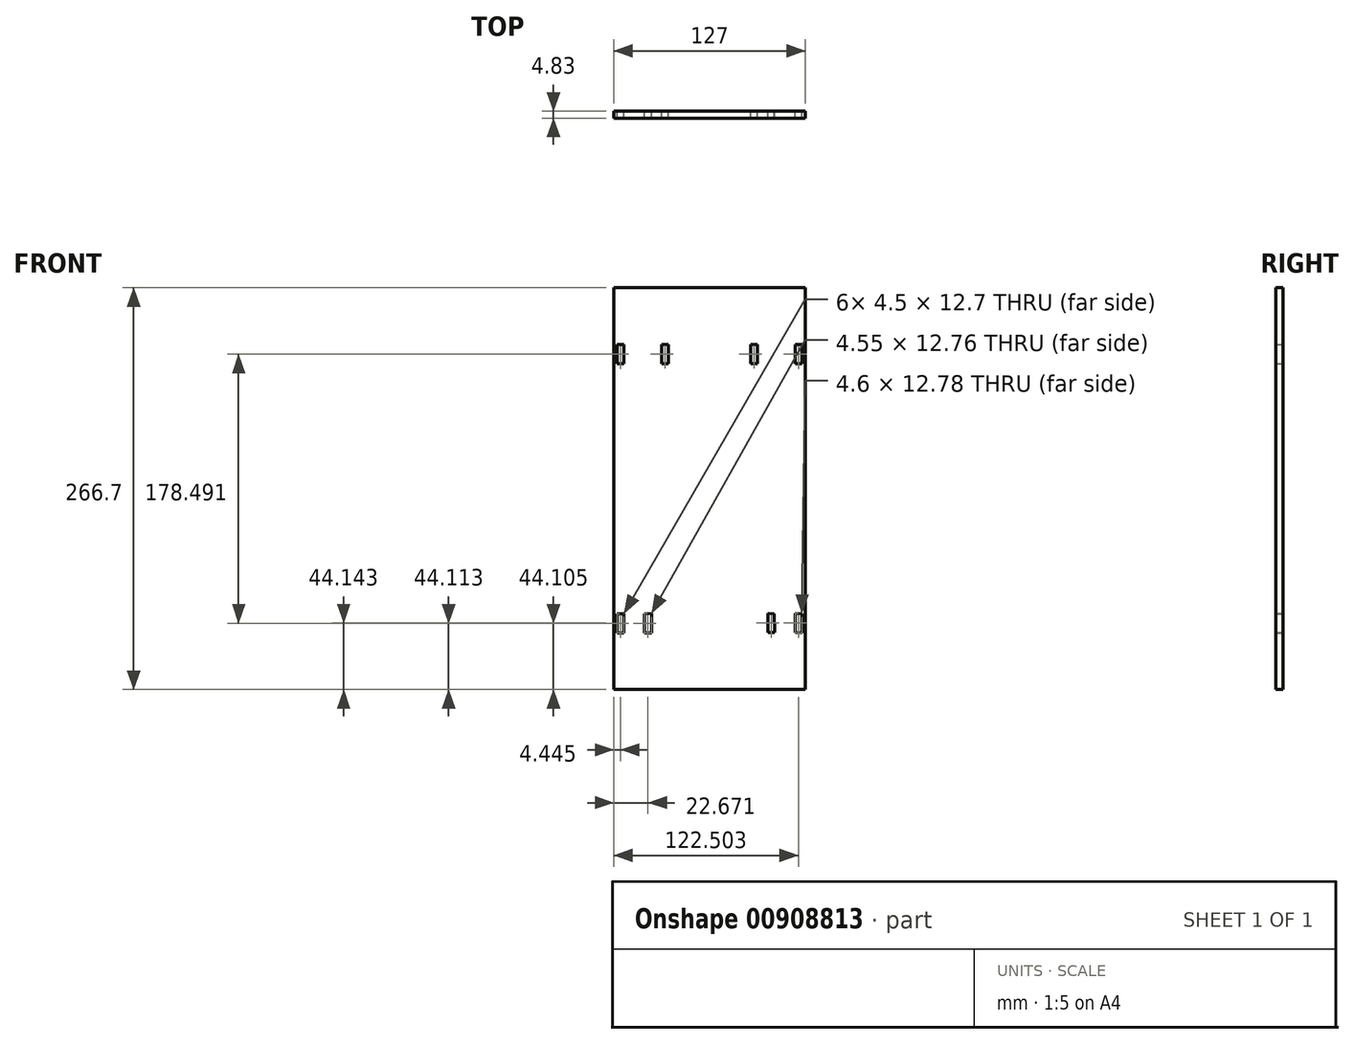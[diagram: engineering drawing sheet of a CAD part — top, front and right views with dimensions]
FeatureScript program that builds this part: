
annotation { "Feature Type Name" : "Feature", "Feature Type Description" : "" }
export const myFeature = defineFeature(function(context is Context, id is Id, definition is map)
    precondition{}
    {
        {
            var Q0;
            Q0=qCreatedBy(makeId("Front.planeOp"),FACE);
            var sketch = newSketch(context, id + "F0", { "sketchPlane" : qUnion([Q0])});
            skLineSegment(sketch, "E0.bottom", {"start": v(63.5, -100.58) * mm, "end": v(-63.5, -100.58) * mm});
            skLineSegment(sketch, "E0.top", {"start": v(63.5, 166.12) * mm, "end": v(-63.5, 166.12) * mm});
            skLineSegment(sketch, "E0.left", {"start": v(63.5, -100.58) * mm, "end": v(63.5, 166.12) * mm});
            skLineSegment(sketch, "E0.right", {"start": v(-63.5, -100.58) * mm, "end": v(-63.5, 166.12) * mm});
            skLineSegment(sketch, "E1.bottom", {"start": v(-61.3, 115.67) * mm, "end": v(-56.8, 115.67) * mm});
            skLineSegment(sketch, "E1.top", {"start": v(-61.3, 128.37) * mm, "end": v(-56.8, 128.37) * mm});
            skLineSegment(sketch, "E1.left", {"start": v(-61.3, 115.67) * mm, "end": v(-61.3, 128.37) * mm});
            skLineSegment(sketch, "E1.right", {"start": v(-56.8, 115.67) * mm, "end": v(-56.8, 128.37) * mm});
            skPoint(sketch, "E1.middle", {"position": v(-59.05, 122.02) * mm});
            skPoint(sketch, "E2", {"position": v(-63.5, 32.77) * mm});
            skPoint(sketch, "E3", {"position": v(-63.5, 99.44) * mm});
            skPoint(sketch, "E4", {"position": v(-63.5, -33.9) * mm});
            skPoint(sketch, "E5", {"position": v(63.5, 32.77) * mm});
            skPoint(sketch, "E6", {"position": v(63.5, 99.44) * mm});
            skPoint(sketch, "E7", {"position": v(63.5, -33.9) * mm});
            skLineSegment(sketch, "E8.MirrorCS", {"start": v(61.3, 128.37) * mm, "end": v(56.8, 128.37) * mm});
            skLineSegment(sketch, "E9.MirrorCS", {"start": v(61.3, 115.67) * mm, "end": v(61.3, 128.37) * mm});
            skLineSegment(sketch, "E10.MirrorCS", {"start": v(56.8, 115.67) * mm, "end": v(56.8, 128.37) * mm});
            skLineSegment(sketch, "E11.MirrorCS", {"start": v(61.3, 115.67) * mm, "end": v(56.8, 115.67) * mm});
            skLineSegment(sketch, "E12.MirrorCS", {"start": v(-61.3, -62.83) * mm, "end": v(-56.8, -62.83) * mm});
            skLineSegment(sketch, "E13.MirrorCS", {"start": v(-61.3, -50.13) * mm, "end": v(-61.3, -62.83) * mm});
            skLineSegment(sketch, "E14.MirrorCS", {"start": v(-56.8, -50.13) * mm, "end": v(-56.8, -62.83) * mm});
            skLineSegment(sketch, "E15.MirrorCS", {"start": v(-61.3, -50.13) * mm, "end": v(-56.8, -50.13) * mm});
            skLineSegment(sketch, "E16.MirrorCS", {"start": v(56.7, -50.05) * mm, "end": v(56.86, -62.75) * mm});
            skLineSegment(sketch, "E17.MirrorCS", {"start": v(61.3, -62.83) * mm, "end": v(56.86, -62.75) * mm});
            skLineSegment(sketch, "E18.MirrorCS", {"start": v(61.3, -50.13) * mm, "end": v(61.3, -62.83) * mm});
            skLineSegment(sketch, "E19.MirrorCS", {"start": v(61.3, -50.13) * mm, "end": v(56.7, -50.05) * mm});
            skLineSegment(sketch, "E20.bottom", {"start": v(-31.7, 115.88) * mm, "end": v(-27.2, 115.88) * mm});
            skLineSegment(sketch, "E20.top", {"start": v(-31.7, 128.58) * mm, "end": v(-27.2, 128.58) * mm});
            skLineSegment(sketch, "E20.left", {"start": v(-31.7, 115.88) * mm, "end": v(-31.7, 128.58) * mm});
            skLineSegment(sketch, "E20.right", {"start": v(-27.2, 115.88) * mm, "end": v(-27.2, 128.58) * mm});
            skLineSegment(sketch, "E21.MirrorCS", {"start": v(31.7, 128.58) * mm, "end": v(27.2, 128.58) * mm});
            skLineSegment(sketch, "E22.MirrorCS", {"start": v(31.7, 115.88) * mm, "end": v(31.7, 128.58) * mm});
            skLineSegment(sketch, "E23.MirrorCS", {"start": v(27.2, 115.88) * mm, "end": v(27.2, 128.58) * mm});
            skLineSegment(sketch, "E24.MirrorCS", {"start": v(31.7, 115.88) * mm, "end": v(27.2, 115.88) * mm});
            skLineSegment(sketch, "E25.MirrorCS", {"start": v(-43.1, -50.15) * mm, "end": v(-38.55, -50.09) * mm});
            skLineSegment(sketch, "E26.MirrorCS", {"start": v(-38.55, -50.09) * mm, "end": v(-38.55, -62.85) * mm});
            skLineSegment(sketch, "E27.MirrorCS", {"start": v(-43.1, -62.85) * mm, "end": v(-38.55, -62.85) * mm});
            skLineSegment(sketch, "E28.MirrorCS", {"start": v(-43.1, -50.15) * mm, "end": v(-43.1, -62.85) * mm});
            skLineSegment(sketch, "E29.MirrorCS", {"start": v(43, -50.15) * mm, "end": v(43.16, -62.74) * mm});
            skLineSegment(sketch, "E30.MirrorCS", {"start": v(38.66, -50.04) * mm, "end": v(38.66, -62.74) * mm});
            skLineSegment(sketch, "E31.MirrorCS", {"start": v(43.16, -62.74) * mm, "end": v(38.66, -62.74) * mm});
            skLineSegment(sketch, "E32.MirrorCS", {"start": v(43, -50.15) * mm, "end": v(38.66, -50.04) * mm});
            skSolve(sketch);
        }
        {
            var Q0;
            Q0=makeQuery(id+"F0.imprint","IMPRINT",FACE,{"disambiguationData":[TD([[makeQuery(id+"F0.imprint","IMPRINT",EDGE,{"derivedFrom":sQuery(id+"F0.wireOp",EDGE,"E1.bottom")}),-1.0]])]});
            var Q1;
            Q1=makeQuery(id+"F0.imprint","IMPRINT",FACE,{"disambiguationData":[TD([[makeQuery(id+"F0.imprint","IMPRINT",EDGE,{"derivedFrom":sQuery(id+"F0.wireOp",EDGE,"E8.MirrorCS")}),-1.0]])]});
            var Q2;
            Q2=makeQuery(id+"F0.imprint","IMPRINT",FACE,{"disambiguationData":[TD([[makeQuery(id+"F0.imprint","IMPRINT",EDGE,{"derivedFrom":sQuery(id+"F0.wireOp",EDGE,"E16.MirrorCS")}),-1.0]])]});
            var Q3;
            Q3=makeQuery(id+"F0.imprint","IMPRINT",FACE,{"disambiguationData":[TD([[makeQuery(id+"F0.imprint","IMPRINT",EDGE,{"derivedFrom":sQuery(id+"F0.wireOp",EDGE,"E12.MirrorCS")}),-1.0]])]});
            extrude(context, id + "F1", {"entities" : qUnion([Q0, Q1, Q2, Q3]), "depth" : 4.83 * mm, "offsetDistance" : 25.4 * mm});
        }
    });
